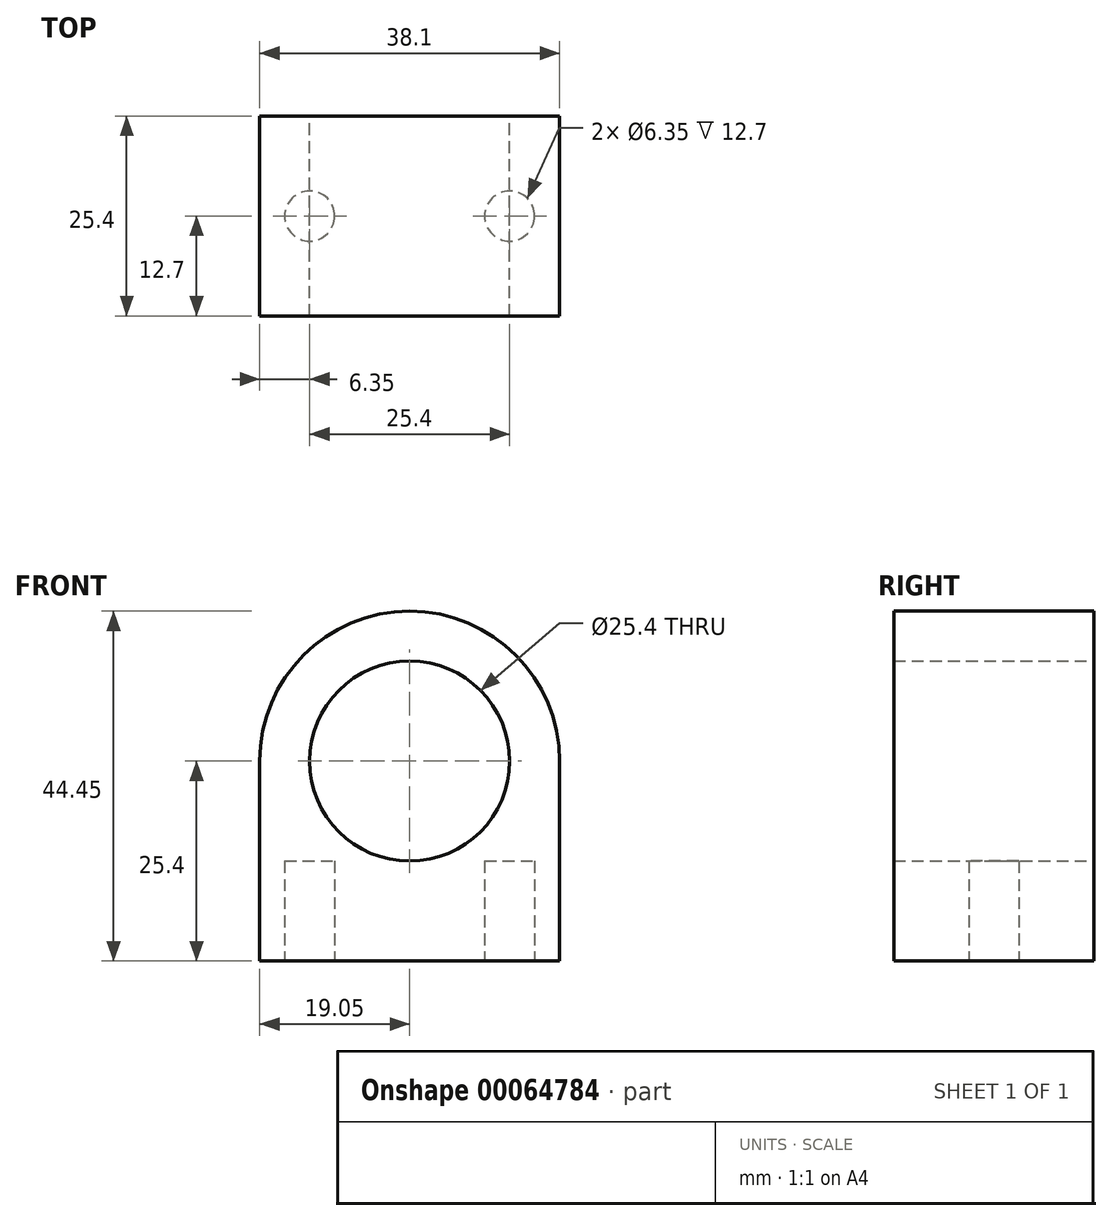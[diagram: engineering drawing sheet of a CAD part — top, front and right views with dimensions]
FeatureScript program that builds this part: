
annotation { "Feature Type Name" : "Feature", "Feature Type Description" : "" }
export const myFeature = defineFeature(function(context is Context, id is Id, definition is map)
    precondition{}
    {
        {
            var Q0;
            Q0=qCreatedBy(makeId("Front.planeOp"),FACE);
            var sketch = newSketch(context, id + "F0", { "sketchPlane" : qUnion([Q0])});
            skLineSegment(sketch, "E0", {"start": v(-100.63, 0) * mm, "end": v(95.74, 0) * mm, "construction": true});
            skLineSegment(sketch, "E1", {"start": v(0, 105.7) * mm, "end": v(0, -86.48) * mm, "construction": true});
            skCircle(sketch, "E2", {"center": v(0, 25.4) * mm, "radius": 12.7 * mm});
            skArc(sketch, "E3", {"start": v(19.05, 25.4) * mm, "mid": v(0, 44.45) * mm, "end": v(-19.05, 25.4) * mm});
            skLineSegment(sketch, "E4", {"start": v(-19.05, 25.4) * mm, "end": v(-19.05, 0) * mm});
            skLineSegment(sketch, "E5", {"start": v(19.05, 25.4) * mm, "end": v(19.05, 0) * mm});
            skLineSegment(sketch, "E6", {"start": v(19.05, 0) * mm, "end": v(-19.05, 0) * mm});
            skSolve(sketch);
        }
        {
            var Q0;
            Q0=qSketchRegion(id+"F0",true);
            extrude(context, id + "F1", {"entities" : qUnion([Q0]), "endBound" : BoundingType.SYMMETRIC, "depth" : 25.4 * mm});
        }
        {
            var Q0;
            Q0=makeQuery(id+"F1.opExtrude","SWEPT_FACE",FACE,{"disambiguationData":[OSD([sQuery(id+"F0.wireOp",EDGE,"E6")])]});
            var sketch = newSketch(context, id + "F2", { "sketchPlane" : qUnion([Q0])});
            skLineSegment(sketch, "E7", {"start": v(-40.05, 0) * mm, "end": v(38.26, 0) * mm, "construction": true});
            skLineSegment(sketch, "E8", {"start": v(0, 41.76) * mm, "end": v(0, -39.8) * mm, "construction": true});
            skLineSegment(sketch, "E9", {"start": v(-12.7, 18.32) * mm, "end": v(-12.7, -25.64) * mm, "construction": true});
            skLineSegment(sketch, "E10", {"start": v(12.7, 18.32) * mm, "end": v(12.7, -25.64) * mm, "construction": true});
            skCircle(sketch, "E11", {"center": v(-12.7, 0) * mm, "radius": 3.18 * mm});
            skCircle(sketch, "E12", {"center": v(12.7, 0) * mm, "radius": 3.18 * mm});
            skSolve(sketch);
        }
        {
            var Q0;
            Q0=qSketchRegion(id+"F2",true);
            extrude(context, id + "F3", {"entities" : qUnion([Q0]), "operationType" : NewBodyOperationType.REMOVE, "oppositeDirection" : true, "depth" : 12.7 * mm});
        }
    });
